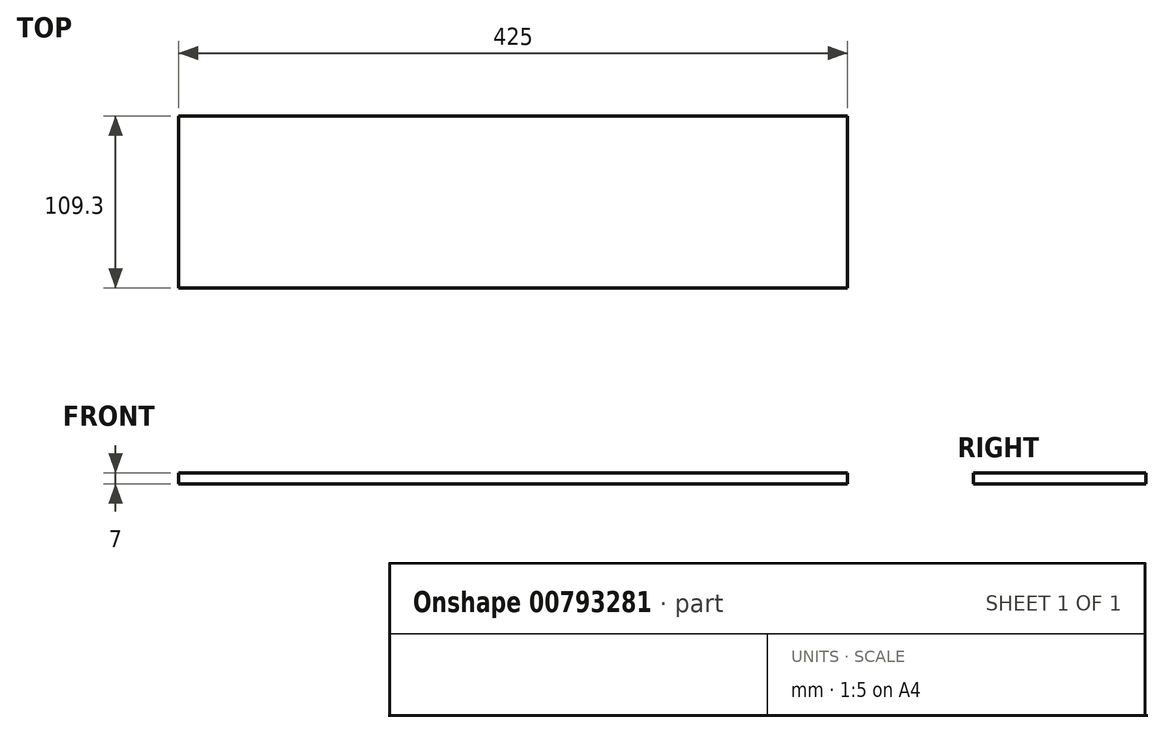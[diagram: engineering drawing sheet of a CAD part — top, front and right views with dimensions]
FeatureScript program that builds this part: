
annotation { "Feature Type Name" : "Feature", "Feature Type Description" : "" }
export const myFeature = defineFeature(function(context is Context, id is Id, definition is map)
    precondition{}
    {
        {
            var Q0;
            Q0=qCreatedBy(makeId("Top.planeOp"),FACE);
            var sketch = newSketch(context, id + "F0", { "sketchPlane" : qUnion([Q0])});
            skLineSegment(sketch, "E0.bottom", {"start": v(-212.5, 54.65) * mm, "end": v(212.5, 54.65) * mm});
            skLineSegment(sketch, "E0.top", {"start": v(-212.5, -54.65) * mm, "end": v(212.5, -54.65) * mm});
            skLineSegment(sketch, "E0.left", {"start": v(-212.5, 54.65) * mm, "end": v(-212.5, -54.65) * mm});
            skLineSegment(sketch, "E0.right", {"start": v(212.5, 54.65) * mm, "end": v(212.5, -54.65) * mm});
            skPoint(sketch, "E0.middle", {"position": v(0, 0) * mm});
            skSolve(sketch);
        }
        {
            var Q0;
            Q0=makeQuery(id+"F0.imprint","IMPRINT",FACE,{"disambiguationData":[TD([[makeQuery(id+"F0.imprint","IMPRINT",EDGE,{"derivedFrom":sQuery(id+"F0.wireOp",EDGE,"E0.bottom")}),-1.0]])]});
            extrude(context, id + "F1", {"entities" : qUnion([Q0]), "depth" : 7 * mm, "offsetDistance" : 25 * mm});
        }
    });
